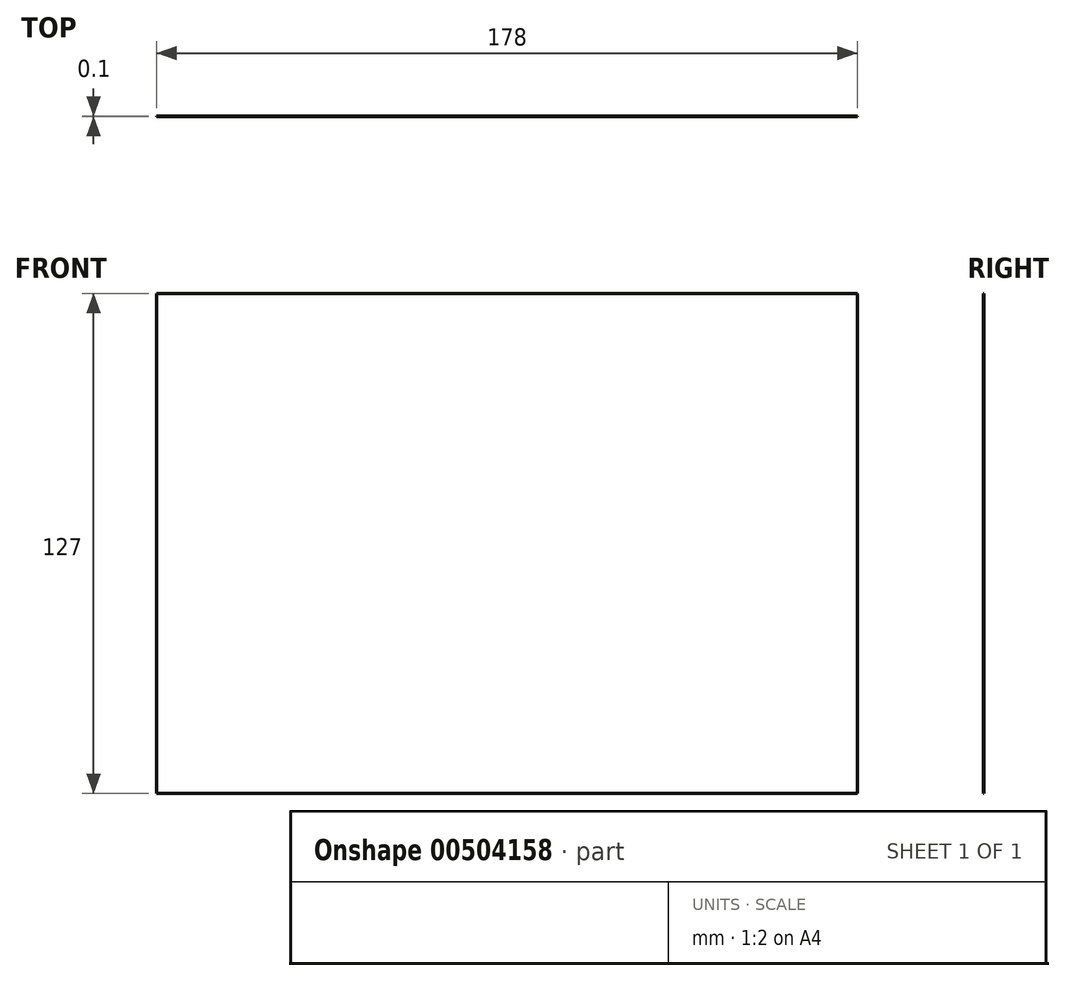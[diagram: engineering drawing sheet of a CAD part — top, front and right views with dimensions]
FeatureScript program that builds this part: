
annotation { "Feature Type Name" : "Feature", "Feature Type Description" : "" }
export const myFeature = defineFeature(function(context is Context, id is Id, definition is map)
    precondition{}
    {
        {
            var Q0;
            Q0=qCreatedBy(makeId("Front.planeOp"),FACE);
            var sketch = newSketch(context, id + "F0", { "sketchPlane" : qUnion([Q0])});
            skLineSegment(sketch, "E0.bottom", {"start": v(89, -63.5) * mm, "end": v(-89, -63.5) * mm});
            skLineSegment(sketch, "E0.top", {"start": v(89, 63.5) * mm, "end": v(-89, 63.5) * mm});
            skLineSegment(sketch, "E0.left", {"start": v(89, -63.5) * mm, "end": v(89, 63.5) * mm});
            skLineSegment(sketch, "E0.right", {"start": v(-89, -63.5) * mm, "end": v(-89, 63.5) * mm});
            skPoint(sketch, "E0.middle", {"position": v(0, 0) * mm});
            skSolve(sketch);
        }
        {
            var Q0;
            Q0 = qSketchRegion(id + "F0", true);
            extrude(context, id + "F1", {"entities" : qUnion([Q0]), "depth" : 0.1 * mm, "offsetDistance" : 25 * mm});
        }
    });
